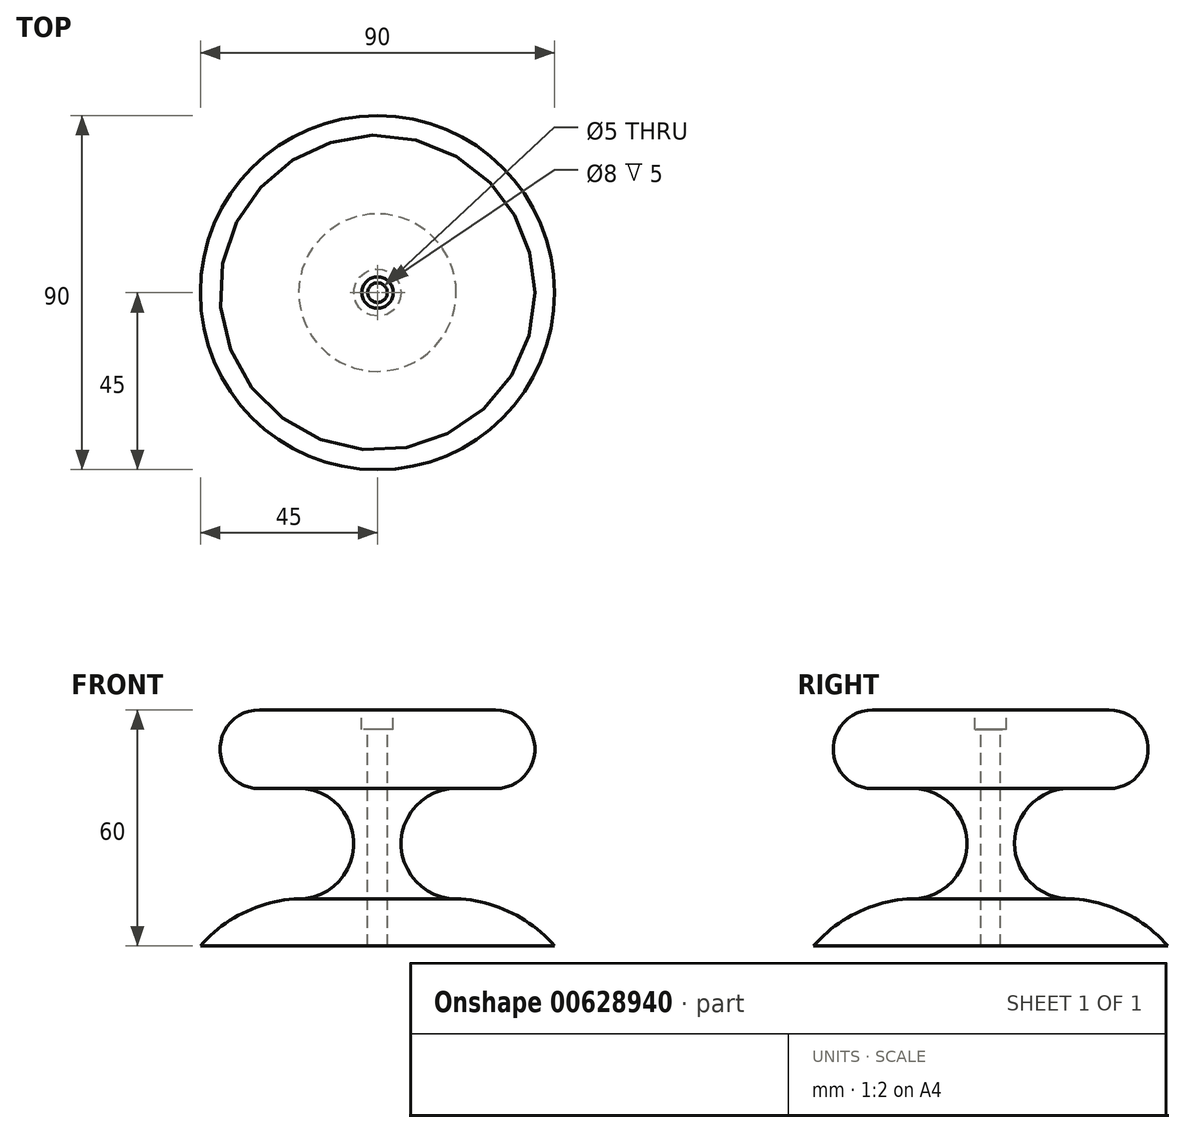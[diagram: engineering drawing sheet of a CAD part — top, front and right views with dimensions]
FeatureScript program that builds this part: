
annotation { "Feature Type Name" : "Feature", "Feature Type Description" : "" }
export const myFeature = defineFeature(function(context is Context, id is Id, definition is map)
    precondition{}
    {
        {
            var Q0;
            Q0=qCreatedBy(makeId("Front.planeOp"),FACE);
            var sketch = newSketch(context, id + "F0", { "sketchPlane" : qUnion([Q0])});
            skArc(sketch, "E0", {"start": v(25, 12) * mm, "mid": v(11.26, 8.58) * mm, "end": v(0, 0) * mm});
            skArc(sketch, "E1", {"start": v(25, 12) * mm, "mid": v(39, 26) * mm, "end": v(25, 40) * mm});
            skLineSegment(sketch, "E2", {"start": v(25, 40) * mm, "end": v(25, 40) * mm});
            skLineSegment(sketch, "E3", {"start": v(15, 40) * mm, "end": v(25, 40) * mm});
            skArc(sketch, "E4", {"start": v(15, 60) * mm, "mid": v(5, 50) * mm, "end": v(15, 40) * mm});
            skLineSegment(sketch, "E5", {"start": v(45, 99.3) * mm, "end": v(45, 0) * mm, "construction": true});
            skLineSegment(sketch, "E6", {"start": v(15, 60) * mm, "end": v(45, 60) * mm});
            skLineSegment(sketch, "E7", {"start": v(45, 0) * mm, "end": v(0, 0) * mm});
            skLineSegment(sketch, "E8", {"start": v(45, 60) * mm, "end": v(45, 0) * mm});
            skSolve(sketch);
        }
        {
            var Q0;
            Q0=makeQuery(id+"F0.imprint","IMPRINT",FACE,{"disambiguationData":[TD([[makeQuery(id+"F0.imprint","IMPRINT",EDGE,{"derivedFrom":sQuery(id+"F0.wireOp",EDGE,"E0")}),1.0]])]});
            var Q1;
            Q1=sQuery(id+"F0.wireOp",EDGE,"E5");
            revolve(context, id + "F1", {"surfaceOperationType" : NewSurfaceOperationType.NEW, "entities" : qUnion([Q0]), "axis" : qUnion([Q1]), "revolveType" : RevolveType.FULL});
        }
        {
            var Q0;
            Q0=makeQuery(id+"F1.opRevolve","SWEPT_FACE",FACE,{"disambiguationData":[OSD([sQuery(id+"F0.wireOp",EDGE,"E6")])]});
            var sketch = newSketch(context, id + "F2", { "sketchPlane" : qUnion([Q0])});
            skPoint(sketch, "E9", {"position": v(45, 0) * mm});
            skSolve(sketch);
        }
        {
            var Q0;
            Q0=sQuery(id+"F2.wireOp",VERTEX,"E9");
            var Q1;
            Q1=makeQuery(id+"F1.opRevolve","SWEPT_BODY",BODY,{"disambiguationData":[OSD([sQuery(id+"F0.wireOp",EDGE,"E0"),sQuery(id+"F0.wireOp",EDGE,"ea6760a3-e37a-456f-9fb7-0b5f88f61a2e"),sQuery(id+"F0.wireOp",EDGE,"E1"),sQuery(id+"F0.wireOp",EDGE,"E3"),sQuery(id+"F0.wireOp",EDGE,"E4"),sQuery(id+"F0.wireOp",EDGE,"E6"),sQuery(id+"F0.wireOp",EDGE,"E7"),sQuery(id+"F0.wireOp",EDGE,"E8")])]});
            hole(context, id + "F3", {"style" : HoleStyle.C_BORE, "endStyle" : HoleEndStyle.THROUGH, "holeDiameter" : 5 * mm, "cBoreDiameter" : 8 * mm, "cBoreDepth" : 5 * mm, "majorDiameter" : 5 * mm, "isTappedThrough" : true, "tappedDepth" : 12 * mm, "tapClearance" : 3, "locations" : qUnion([Q0]), "scope" : qUnion([Q1])});
        }
    });
